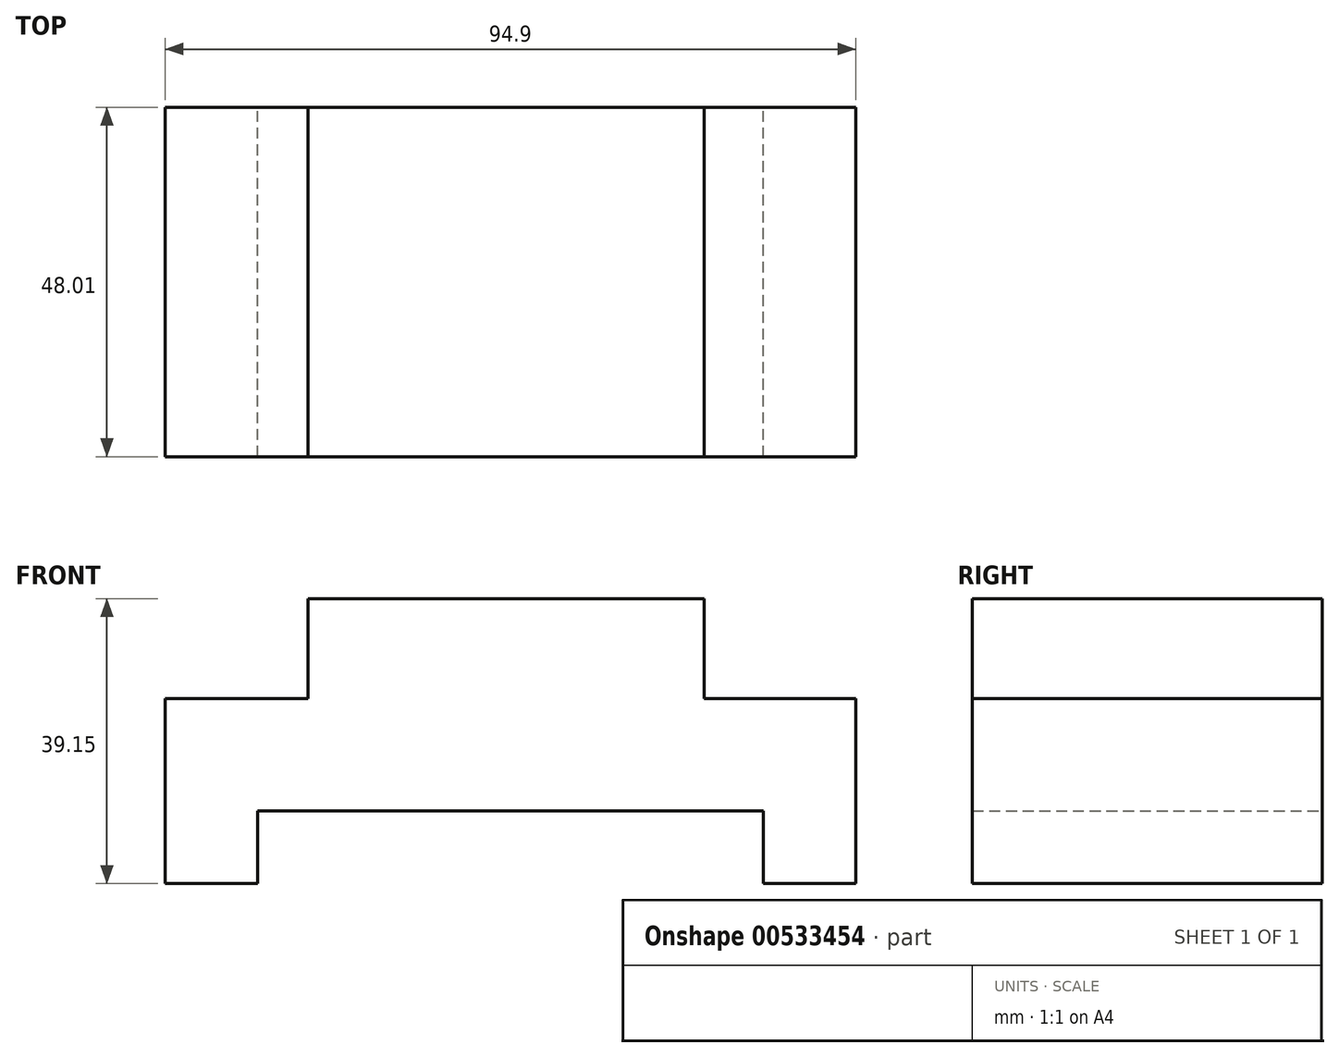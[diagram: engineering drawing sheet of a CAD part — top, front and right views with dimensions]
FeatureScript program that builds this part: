
annotation { "Feature Type Name" : "Feature", "Feature Type Description" : "" }
export const myFeature = defineFeature(function(context is Context, id is Id, definition is map)
    precondition{}
    {
        {
            var Q0;
            Q0=qCreatedBy(makeId("Front.planeOp"),FACE);
            var sketch = newSketch(context, id + "F0", { "sketchPlane" : qUnion([Q0])});
            skLineSegment(sketch, "E0", {"start": v(0, 0) * mm, "end": v(0, 16.66) * mm, "construction": true});
            skLineSegment(sketch, "E1", {"start": v(0, 16.66) * mm, "end": v(0, -17.67) * mm, "construction": true});
            skLineSegment(sketch, "E2", {"start": v(-28.07, 0) * mm, "end": v(-28.07, 13.75) * mm});
            skLineSegment(sketch, "E3", {"start": v(-28.07, 13.75) * mm, "end": v(26.3, 13.75) * mm});
            skLineSegment(sketch, "E4", {"start": v(26.3, 13.75) * mm, "end": v(26.3, 0) * mm});
            skLineSegment(sketch, "E5", {"start": v(26.3, 0) * mm, "end": v(47.19, 0) * mm});
            skLineSegment(sketch, "E6", {"start": v(47.19, 0) * mm, "end": v(47.19, -25.4) * mm});
            skLineSegment(sketch, "E7", {"start": v(47.19, -25.4) * mm, "end": v(34.49, -25.4) * mm});
            skLineSegment(sketch, "E8", {"start": v(-35, -25.4) * mm, "end": v(-47.7, -25.4) * mm});
            skLineSegment(sketch, "E9", {"start": v(-47.7, -25.4) * mm, "end": v(-47.7, 0) * mm});
            skLineSegment(sketch, "E10", {"start": v(-47.7, 0) * mm, "end": v(-28.07, 0) * mm});
            skLineSegment(sketch, "E11", {"start": v(-35, -15.44) * mm, "end": v(34.49, -15.44) * mm});
            skLineSegment(sketch, "E12", {"start": v(-35, -15.44) * mm, "end": v(-35, -25.4) * mm});
            skLineSegment(sketch, "E13", {"start": v(34.49, -15.44) * mm, "end": v(34.49, -25.4) * mm});
            skSolve(sketch);
        }
        {
            var Q0;
            Q0=makeQuery(id+"F0.imprint","IMPRINT",FACE,{"disambiguationData":[TD([[makeQuery(id+"F0.imprint","IMPRINT",EDGE,{"derivedFrom":sQuery(id+"F0.wireOp",EDGE,"E2")}),-1.0]])]});
            extrude(context, id + "F1", {"entities" : qUnion([Q0]), "depth" : 48 * mm, "offsetDistance" : 25.4 * mm});
        }
    });
